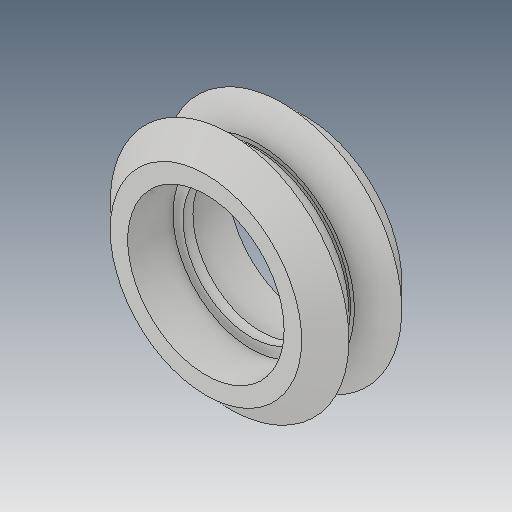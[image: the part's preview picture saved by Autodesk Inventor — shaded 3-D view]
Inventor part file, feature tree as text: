
AUTODESK INVENTOR PART (.ipt)
format: ipt  version: 2017 (Build 210142000, 142)  size: 177,152 bytes
history: native  units: mm
features: sketch x5, extrude x4, revolve x1
ambient origin geometry x8: Origin, YZ Plane, XZ Plane, XY Plane, X Axis, Y Axis, Z Axis, Center Point
bodies: Solid1 (feature_tree)
feature tree (10):
  extrude  "Extrusion1"  Depth=10.23mm TaperAngle=0.0deg
  revolve  "Revolution1"  [1 undecoded]
  extrude  "Extrusion2"  TaperAngle=90.0deg  [1 undecoded]
  extrude  "Extrusion3"  Depth=30.0mm TaperAngle=0.0deg
  extrude  "Extrusion4"  Depth=4.615mm TaperAngle=0.0deg
  sketch  "Sketch1"  dims[d0=24.39mm d1=10.23mm d2=0.0mm]
  sketch  "Sketch2"  dims[d4=0.275mm d5=0.55mm]
  sketch  "Sketch3"  dims[d6=135.0deg d7=90.0deg]
  sketch  "Sketch4"  dims[d8=13.89mm d9=30.0mm d10=0.0mm]
  sketch  "Sketch5"  dims[d11=15.974mm d12=4.615mm d13=0.0mm d14=15.974mm d15=4.615mm d16=0.0mm]
note: 2 required parameter values undecoded (feature->parameter linkage not recoverable at this tier; creation-order binding heuristic only, values carry confidence <= 0.55)